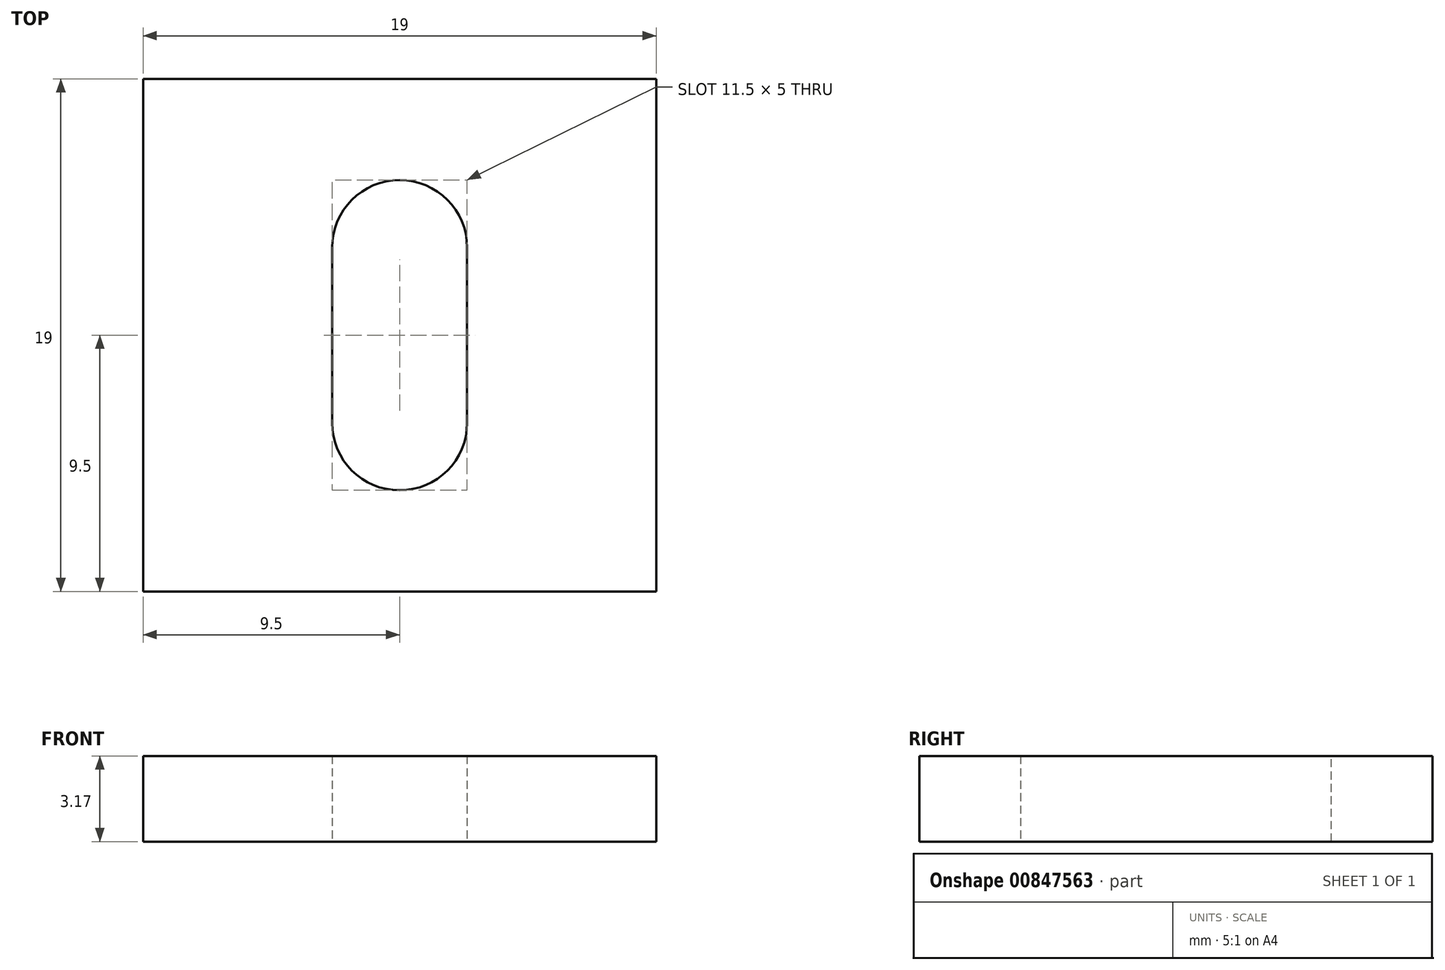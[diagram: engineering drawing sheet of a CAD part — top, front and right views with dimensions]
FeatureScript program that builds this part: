
annotation { "Feature Type Name" : "Feature", "Feature Type Description" : "" }
export const myFeature = defineFeature(function(context is Context, id is Id, definition is map)
    precondition{}
    {
        {
            var Q0;
            Q0=qCreatedBy(makeId("Top.planeOp"),FACE);
            var sketch = newSketch(context, id + "F0", { "sketchPlane" : qUnion([Q0])});
            skLineSegment(sketch, "E0.bottom", {"start": v(9.5, 9.5) * mm, "end": v(-9.5, 9.5) * mm});
            skLineSegment(sketch, "E0.top", {"start": v(9.5, -9.5) * mm, "end": v(-9.5, -9.5) * mm});
            skLineSegment(sketch, "E0.left", {"start": v(9.5, 9.5) * mm, "end": v(9.5, -9.5) * mm});
            skLineSegment(sketch, "E0.right", {"start": v(-9.5, 9.5) * mm, "end": v(-9.5, -9.5) * mm});
            skPoint(sketch, "E0.middle", {"position": v(0, 0) * mm});
            skLineSegment(sketch, "E1.bottom", {"start": v(2.5, 5.75) * mm, "end": v(-2.5, 5.75) * mm});
            skLineSegment(sketch, "E1.top", {"start": v(2.5, -5.75) * mm, "end": v(-2.5, -5.75) * mm});
            skLineSegment(sketch, "E1.left", {"start": v(2.5, 5.75) * mm, "end": v(2.5, -5.75) * mm});
            skLineSegment(sketch, "E1.right", {"start": v(-2.5, 5.75) * mm, "end": v(-2.5, -5.75) * mm});
            skSolve(sketch);
        }
        {
            var Q0;
            Q0=makeQuery(id+"F0.imprint","IMPRINT",FACE,{"disambiguationData":[TD([[makeQuery(id+"F0.imprint","IMPRINT",EDGE,{"derivedFrom":sQuery(id+"F0.wireOp",EDGE,"E0.bottom")}),1.0]])]});
            extrude(context, id + "F1", {"entities" : qUnion([Q0]), "depth" : 3.17 * mm, "offsetDistance" : 25 * mm});
        }
        {
            var Q0;
            Q0=makeQuery(id+"F1.opExtrude","SWEPT_EDGE",EDGE,{"disambiguationData":[OSD([sQuery(id+"F0.wireOp",EDGE,"E1.bottom"),sQuery(id+"F0.wireOp",EDGE,"E1.right")])]});
            var Q1;
            Q1=makeQuery(id+"F1.opExtrude","SWEPT_EDGE",EDGE,{"disambiguationData":[OSD([sQuery(id+"F0.wireOp",EDGE,"E1.top"),sQuery(id+"F0.wireOp",EDGE,"E1.right")])]});
            var Q2;
            Q2=makeQuery(id+"F1.opExtrude","SWEPT_EDGE",EDGE,{"disambiguationData":[OSD([sQuery(id+"F0.wireOp",EDGE,"E1.bottom"),sQuery(id+"F0.wireOp",EDGE,"E1.left")])]});
            var Q3;
            Q3=makeQuery(id+"F1.opExtrude","SWEPT_EDGE",EDGE,{"disambiguationData":[OSD([sQuery(id+"F0.wireOp",EDGE,"E1.top"),sQuery(id+"F0.wireOp",EDGE,"E1.left")])]});
            fillet(context, id + "F2", {"entities" : qUnion([Q0, Q1, Q2, Q3]), "radius" : 2.5 * mm, "tangentPropagation" : true, "allowEdgeOverflow" : false});
        }
    });
